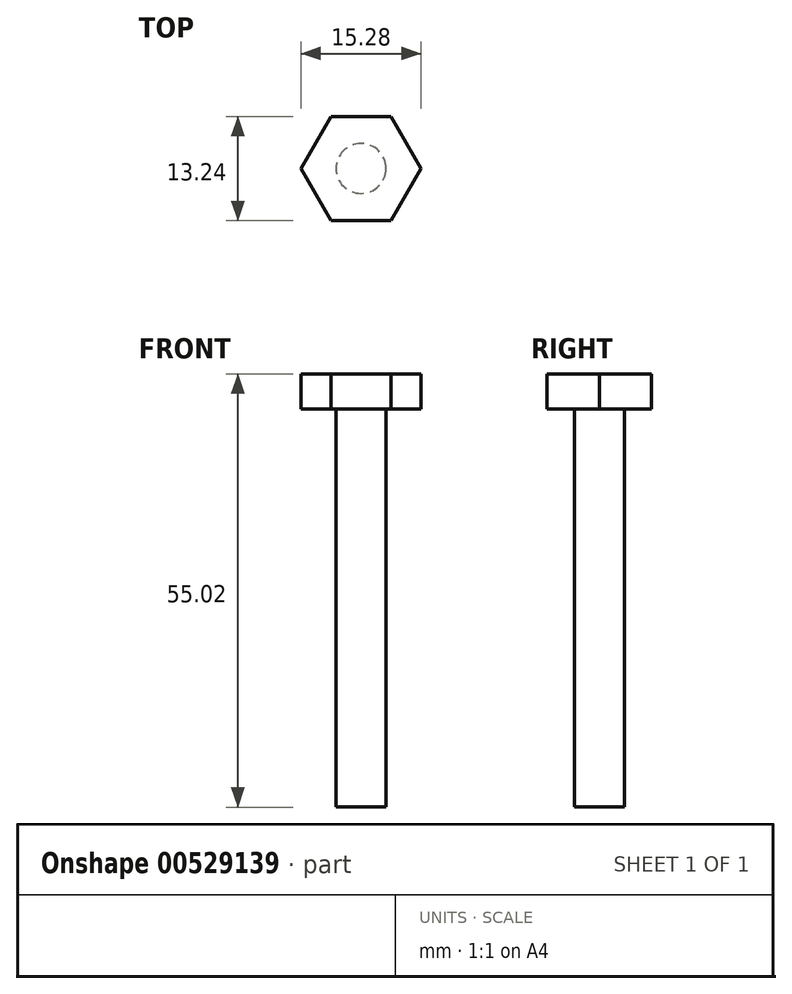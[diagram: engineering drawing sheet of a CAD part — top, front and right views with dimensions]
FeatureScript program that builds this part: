
annotation { "Feature Type Name" : "Feature", "Feature Type Description" : "" }
export const myFeature = defineFeature(function(context is Context, id is Id, definition is map)
    precondition{}
    {
        {
            var Q0;
            Q0=qCreatedBy(makeId("Top.planeOp"),FACE);
            var sketch = newSketch(context, id + "F0", { "sketchPlane" : qUnion([Q0])});
            skCircle(sketch, "E0.cCircle", {"center": v(0, 0) * mm, "radius": 6.62 * mm, "construction": true});
            skLineSegment(sketch, "E0.0", {"start": v(-3.82, 6.62) * mm, "end": v(3.82, 6.62) * mm});
            skLineSegment(sketch, "E0.1", {"start": v(3.82, 6.62) * mm, "end": v(7.64, 0) * mm});
            skLineSegment(sketch, "E0.2", {"start": v(7.64, 0) * mm, "end": v(3.82, -6.62) * mm});
            skLineSegment(sketch, "E0.3", {"start": v(3.82, -6.62) * mm, "end": v(-3.82, -6.62) * mm});
            skLineSegment(sketch, "E0.4", {"start": v(-3.82, -6.62) * mm, "end": v(-7.64, 0) * mm});
            skLineSegment(sketch, "E0.5", {"start": v(-7.64, 0) * mm, "end": v(-3.82, 6.62) * mm});
            skPoint(sketch, "E0.0.midPoint", {"position": v(0, 6.62) * mm});
            skSolve(sketch);
        }
        {
            var Q0;
            Q0 = qSketchRegion(id + "F0", true);
            extrude(context, id + "F1", {"entities" : qUnion([Q0]), "depth" : 4.47 * mm, "offsetDistance" : 25.4 * mm});
        }
        {
            var Q0;
            Q0=makeQuery(id+"F1.opExtrude","CAP_FACE",FACE,{"disambiguationData":[OSD([sQuery(id+"F0.wireOp",EDGE,"E0.0"),sQuery(id+"F0.wireOp",EDGE,"E0.1"),sQuery(id+"F0.wireOp",EDGE,"E0.2"),sQuery(id+"F0.wireOp",EDGE,"E0.3"),sQuery(id+"F0.wireOp",EDGE,"E0.4"),sQuery(id+"F0.wireOp",EDGE,"E0.5")])],"isStart":true});
            var sketch = newSketch(context, id + "F2", { "sketchPlane" : qUnion([Q0])});
            skCircle(sketch, "E1", {"center": v(0, 0) * mm, "radius": 3.18 * mm});
            skSolve(sketch);
        }
        {
            var Q0;
            Q0 = qSketchRegion(id + "F2", true);
            extrude(context, id + "F3", {"entities" : qUnion([Q0]), "operationType" : NewBodyOperationType.ADD, "depth" : 50.55 * mm, "offsetDistance" : 25.4 * mm});
        }
    });
